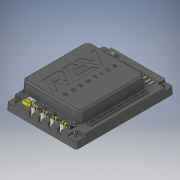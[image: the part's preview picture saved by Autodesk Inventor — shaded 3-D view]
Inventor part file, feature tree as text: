
AUTODESK INVENTOR PART (.ipt)
format: ipt  version: 2017.3 (Build 213256000, 256)  size: 4,917,248 bytes
history: native  units: in
note: dims shown in document units (in); Inventor stores cm internally (conversion verified against a paired STEP export)
features: other x42, sketch x3
ambient origin geometry x8: Origin, YZ Plane, XZ Plane, XY Plane, X Axis, Y Axis, Z Axis, Center Point
bodies: Solid1 (feature_tree), Solid2 (feature_tree), Solid3 (feature_tree), Solid4 (feature_tree), Solid5 (feature_tree), Solid6 (feature_tree), Solid7 (feature_tree), Solid8 (feature_tree), Solid9 (feature_tree), Solid10 (feature_tree), Solid11 (feature_tree), Solid12 (feature_tree), Solid13 (feature_tree), Solid14 (feature_tree), Solid15 (feature_tree), Solid16 (feature_tree), Solid17 (feature_tree), Solid18 (feature_tree), Solid19 (feature_tree), Solid20 (feature_tree), Solid21 (feature_tree), Solid22 (feature_tree), Solid23 (feature_tree), Solid24 (feature_tree), Solid25 (feature_tree), Solid26 (feature_tree), Solid27 (feature_tree), Solid28 (feature_tree), Solid29 (feature_tree), Solid30 (feature_tree), Solid31 (feature_tree), Solid32 (feature_tree)
feature tree (45):
  sketch  "Sketch1"
  other  "Batt_Pos"
  sketch  "Sketch2"
  other  "Batt_Neg"
  other  "Motor_0_Pos"
  other  "Motor_0_Neg"
  other  "Motor_1_Pos"
  other  "Motor_1_Neg"
  other  "Motor_2_Pos"
  other  "Motor_2_Neg"
  other  "Motor_3_Pos"
  other  "Motor_3_Neg"
  sketch  "Sketch3"
  other  "REV-30012-002-1-solid1"
  other  "REV-30012-222-1-solid1"
  other  "REV-50012-002-1-solid1"
  other  "REV-50012-002-1-solid2"
  other  "REV-30012-003-1-solid1"
  other  "REV-50012-001-1_REV-50012-090-1-solid1"
  other  "REV-50012-001-1_JST-B4B-PH-K-S-1-solid1"
  other  "REV-50012-001-1_JST-B4B-PH-K-S-2-solid1"
  other  "REV-50012-001-1_JST-B4B-PH-K-S-3-solid1"
  other  "REV-50012-001-1_JST-B4B-PH-K-S-4-solid1"
  other  "REV-50012-001-1_JST-B4B-PH-K-S-5-solid1"
  other  "REV-50012-001-1_JST-B4B-PH-K-S-6-solid1"
  other  "REV-50012-001-1_JST-B4B-PH-K-S-7-solid1"
  other  "REV-50012-001-1_JST-B4B-PH-K-S-8-solid1"
  other  "REV-50012-001-1_JST-B4B-PH-K-S-9-solid1"
  other  "REV-50012-001-1_JST-B4B-PH-K-S-10-solid1"
  other  "REV-50012-001-1_JST-B3B-PH-K-S-1-solid1"
  other  "REV-50012-001-1_JST-B3B-PH-K-S-2-solid1"
  other  "REV-50012-001-1_JST-B3B-PH-K-S-3-solid1"
  other  "REV-50012-001-1_JST-B3B-PH-K-S-4-solid1"
  other  "REV-50012-001-1_EDAC_690-005-299-043-1-solid1"
  other  "REV-50012-001-1_WFD-PZ2_54-32AT-2_5MM-1-solid1"
  other  "REV-50012-001-1_AMASS_XT30UPB-F-1-solid1"
  other  "REV-50012-001-1_JST-B4B-PH-K-S-11-solid1"
  other  "REV-50012-001-1_JST-B4B-PH-K-S-12-solid1"
  other  "REV-50012-001-1_JST-B4B-PH-K-S-13-solid1"
  other  "REV-50012-001-1_JST-B4B-PH-K-S-14-solid1"
  other  "REV-50012-001-1_AMASS_XT30UPB-M-1-solid1"
  other  "REV-50012-001-1_JST-B2P-VH-1-solid1"
  other  "REV-50012-001-1_JST-B2P-VH-2-solid1"
  other  "REV-50012-001-1_JST-B2P-VH-3-solid1"
  other  "REV-50012-001-1_JST-B2P-VH-4-solid1"
